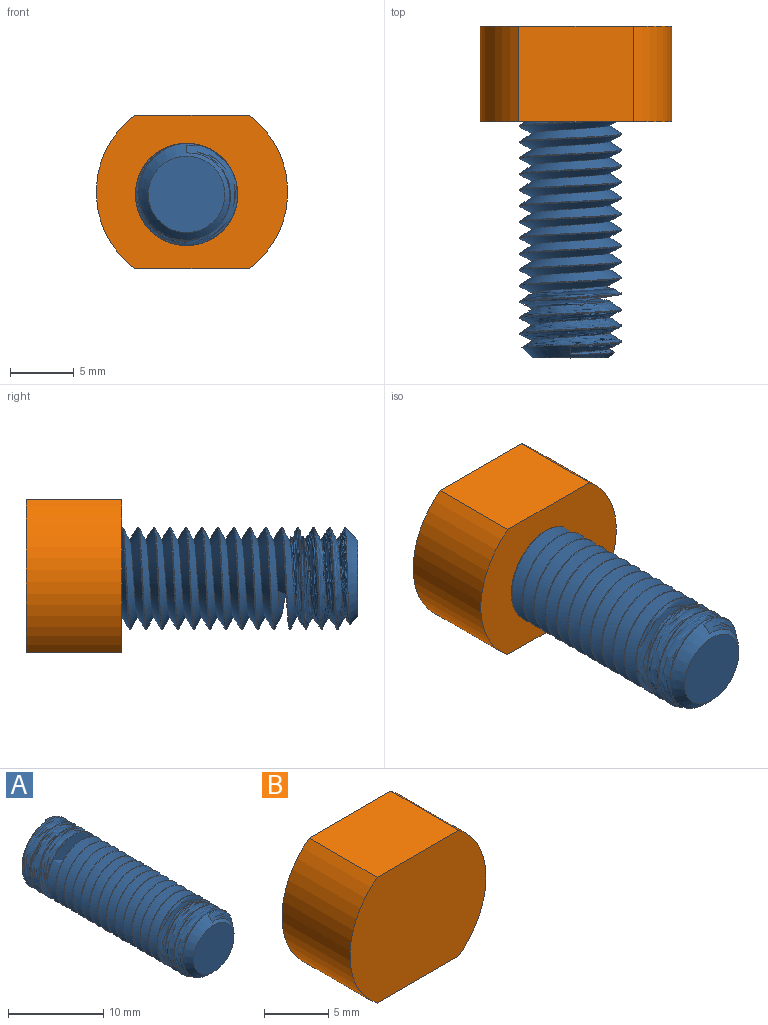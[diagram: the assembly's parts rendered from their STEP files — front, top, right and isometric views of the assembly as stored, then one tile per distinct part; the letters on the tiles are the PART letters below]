
ASSEMBLY  parts=2 mates=1
PART A: 8 faces, bbox 9.3x26x8 mm
  f0: cylinder r=4mm len=24mm, axis (0,1,0), area -36.2mm2, adj f2,f3,f4,f5,f6
  f1: plane 6x6mm, normal (0,-1,0), area 28.3mm2, adj f3
  f2: plane 7.47x7.18mm, normal (0,1,0), area 40.5mm2, adj f0,f4,f5,f6
  f3: cone r=3mm half-angle=45deg, axis (0,1,0), area 18.7mm2, adj f0,f1,f5,f6,f7
  f4: plane 0.39x0.27mm, normal (-1,0,-0.03), area 0mm2, adj f0,f2,f5
  f5: bspline ~25.66x8.01mm, area 512.3mm2, adj f0,f2,f3,f4,f6,f7
  f6: bspline ~25.32x9.25mm, area 476.7mm2, adj f0,f2,f3,f5,f7
  f7: plane 0.83x0.6mm, normal (1,0,0.03), area 0.1mm2, adj f3,f5,f6
PART B: 6 faces, bbox 15x7.5x12 mm
  f0: plane 9x7.5mm, normal (0,0,-1), area 67.5mm2, adj f1,f3,f4,f5
  f1: cylinder r=7.5mm len=12mm, axis (0,1,0), area 104.3mm2, adj f0,f2,f4,f5
  f2: plane 9x7.5mm, normal (0,0,1), area 67.5mm2, adj f1,f3,f4,f5
  f3: cylinder r=7.5mm len=12mm, axis (0,1,0), area 104.3mm2, adj f0,f2,f4,f5
  f4: plane 15x12mm, normal (0,-1,0), area 158.3mm2, adj f0,f1,f2,f3
  f5: plane 15x12mm, normal (0,1,0), area 158.3mm2, adj f0,f1,f2,f3
PLACE A t=(-29.71,-5,-0.56)mm
PLACE B t=(1.99,-4,-0.38)mm
MATE fastened A.f2 <-> B.f1  axis (0,1,0) through (1.99,-5,-0.38)mm
